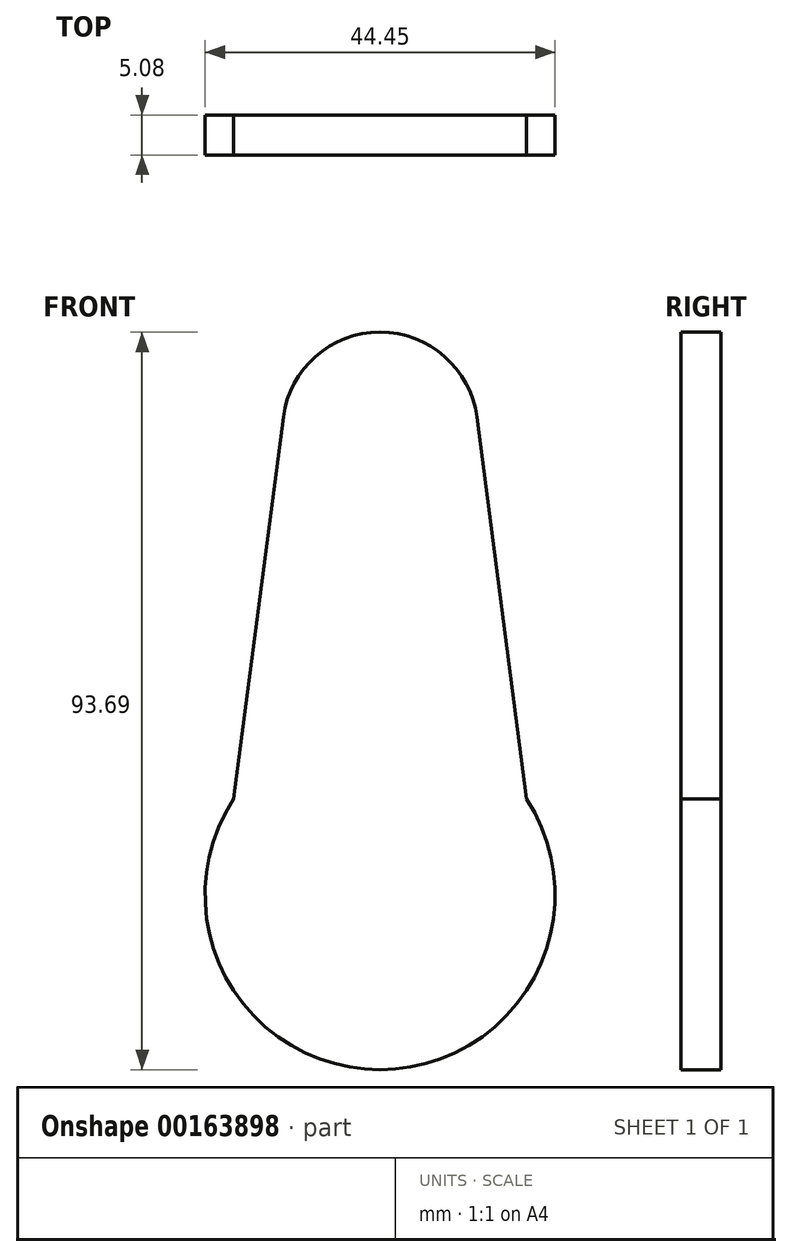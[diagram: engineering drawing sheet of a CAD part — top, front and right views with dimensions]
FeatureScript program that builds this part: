
annotation { "Feature Type Name" : "Feature", "Feature Type Description" : "" }
export const myFeature = defineFeature(function(context is Context, id is Id, definition is map)
    precondition{}
    {
        {
            var Q0;
            Q0=qCreatedBy(makeId("Front.planeOp"),FACE);
            var sketch = newSketch(context, id + "F0", { "sketchPlane" : qUnion([Q0])});
            skCircle(sketch, "E0", {"center": v(0, 31.66) * mm, "radius": 12.4 * mm});
            skCircle(sketch, "E1", {"center": v(0, -27.4) * mm, "radius": 22.23 * mm});
            skLineSegment(sketch, "E2", {"start": v(12.3, 33.26) * mm, "end": v(18.6, -15.25) * mm});
            skLineSegment(sketch, "E3", {"start": v(-12.3, 33.26) * mm, "end": v(-18.6, -15.25) * mm});
            skSolve(sketch);
        }
        {
            var Q0;
            {var subQ0=sQuery(id+"F0.wireOp",EDGE,"E1");var subQ1=makeQuery(id+"F0.imprint","INTERSECT",VERTEX,{"derivedFrom":[subQ0,sQuery(id+"F0.wireOp",EDGE,"E2")]});Q0=makeQuery(id+"F0.imprint","IMPRINT",FACE,{"disambiguationData":[TD([[makeQuery(id+"F0.imprint","IMPRINT",EDGE,{"disambiguationData":[TD([[subQ1,-1.0]])],"derivedFrom":subQ0}),1.0]])]});}
            var Q1;
            {var subQ0=sQuery(id+"F0.wireOp",EDGE,"E0");var subQ1=makeQuery(id+"F0.imprint","INTERSECT",VERTEX,{"derivedFrom":[subQ0,sQuery(id+"F0.wireOp",EDGE,"E2")]});Q1=makeQuery(id+"F0.imprint","IMPRINT",FACE,{"disambiguationData":[TD([[makeQuery(id+"F0.imprint","IMPRINT",EDGE,{"disambiguationData":[TD([[subQ1,-1.0]])],"derivedFrom":subQ0}),1.0]])]});}
            var Q2;
            {var subQ0=sQuery(id+"F0.wireOp",EDGE,"E2");Q2=makeQuery(id+"F0.imprint","IMPRINT",FACE,{"disambiguationData":[TD([[makeQuery(id+"F0.imprint","IMPRINT",EDGE,{"derivedFrom":subQ0}),-1.0]])]});}
            extrude(context, id + "F1", {"entities" : qUnion([Q0, Q1, Q2]), "endBound" : BoundingType.SYMMETRIC, "depth" : 5.08 * mm});
        }
    });
